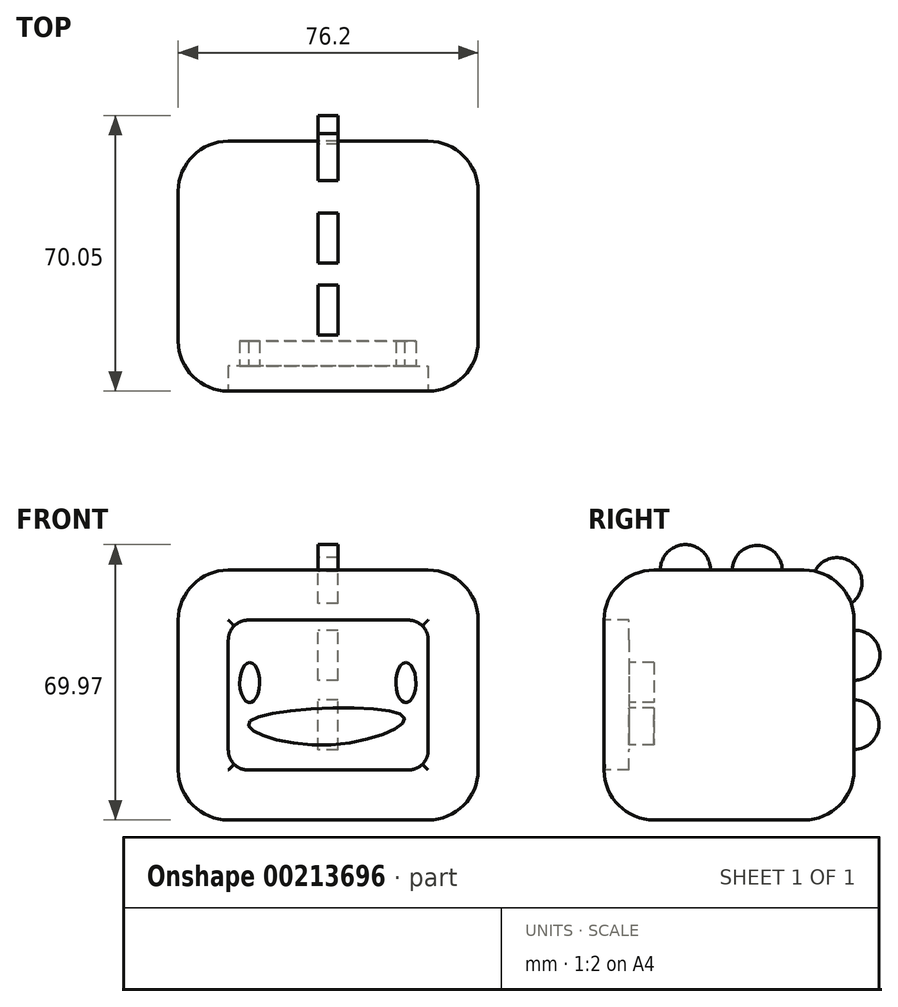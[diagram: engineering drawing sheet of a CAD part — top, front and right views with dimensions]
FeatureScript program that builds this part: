
annotation { "Feature Type Name" : "Feature", "Feature Type Description" : "" }
export const myFeature = defineFeature(function(context is Context, id is Id, definition is map)
    precondition{}
    {
        {
            var Q0;
            Q0=qCreatedBy(makeId("Top.planeOp"),FACE);
            var sketch = newSketch(context, id + "F0", { "sketchPlane" : qUnion([Q0])});
            skLineSegment(sketch, "E0.bottom", {"start": v(25.4, 31.75) * mm, "end": v(-25.4, 31.75) * mm});
            skLineSegment(sketch, "E0.top", {"start": v(25.4, -31.75) * mm, "end": v(-25.4, -31.75) * mm});
            skLineSegment(sketch, "E0.left", {"start": v(38.1, 19.05) * mm, "end": v(38.1, -19.05) * mm});
            skLineSegment(sketch, "E0.right", {"start": v(-38.1, 19.05) * mm, "end": v(-38.1, -19.05) * mm});
            skPoint(sketch, "E0.middle", {"position": v(0, 0) * mm});
            skPoint(sketch, "E1.visualSharp", {"position": v(38.1, -31.75) * mm});
            skArc(sketch, "E1.filletArc", {"start": v(25.4, -31.75) * mm, "mid": v(34.38, -28.03) * mm, "end": v(38.1, -19.05) * mm});
            skPoint(sketch, "E2.visualSharp", {"position": v(38.1, 31.75) * mm});
            skArc(sketch, "E2.filletArc", {"start": v(38.1, 19.05) * mm, "mid": v(34.38, 28.03) * mm, "end": v(25.4, 31.75) * mm});
            skPoint(sketch, "E3.visualSharp", {"position": v(-38.1, 31.75) * mm});
            skArc(sketch, "E3.filletArc", {"start": v(-25.4, 31.75) * mm, "mid": v(-34.38, 28.03) * mm, "end": v(-38.1, 19.05) * mm});
            skPoint(sketch, "E4.visualSharp", {"position": v(-38.1, -31.75) * mm});
            skArc(sketch, "E4.filletArc", {"start": v(-38.1, -19.05) * mm, "mid": v(-34.38, -28.03) * mm, "end": v(-25.4, -31.75) * mm});
            skSolve(sketch);
        }
        {
            var Q0;
            Q0=makeQuery(id+"F0.imprint","IMPRINT",FACE,{"disambiguationData":[TD([[makeQuery(id+"F0.imprint","IMPRINT",EDGE,{"derivedFrom":sQuery(id+"F0.wireOp",EDGE,"E0.bottom")}),1.0]])]});
            extrude(context, id + "F1", {"entities" : qUnion([Q0]), "depth" : 63.5 * mm});
        }
        {
            var Q0;
            Q0=makeQuery(id+"F1.opExtrude","CAP_FACE",FACE,{"disambiguationData":[OSD([sQuery(id+"F0.wireOp",EDGE,"E0.bottom"),sQuery(id+"F0.wireOp",EDGE,"E0.top"),sQuery(id+"F0.wireOp",EDGE,"E0.left"),sQuery(id+"F0.wireOp",EDGE,"E0.right"),sQuery(id+"F0.wireOp",EDGE,"E1.filletArc"),sQuery(id+"F0.wireOp",EDGE,"E2.filletArc"),sQuery(id+"F0.wireOp",EDGE,"E3.filletArc"),sQuery(id+"F0.wireOp",EDGE,"E4.filletArc")])],"isStart":false});
            var Q1;
            Q1=makeQuery(id+"F1.opExtrude","CAP_FACE",FACE,{"disambiguationData":[OSD([sQuery(id+"F0.wireOp",EDGE,"E0.bottom"),sQuery(id+"F0.wireOp",EDGE,"E0.top"),sQuery(id+"F0.wireOp",EDGE,"E0.left"),sQuery(id+"F0.wireOp",EDGE,"E0.right"),sQuery(id+"F0.wireOp",EDGE,"E1.filletArc"),sQuery(id+"F0.wireOp",EDGE,"E2.filletArc"),sQuery(id+"F0.wireOp",EDGE,"E3.filletArc"),sQuery(id+"F0.wireOp",EDGE,"E4.filletArc")])],"isStart":true});
            fillet(context, id + "F2", {"entities" : qUnion([Q0, Q1]), "radius" : 12.7 * mm, "tangentPropagation" : true, "allowEdgeOverflow" : false});
        }
        {
            var Q0;
            Q0=makeQuery(id+"F1.opExtrude","SWEPT_FACE",FACE,{"disambiguationData":[OSD([sQuery(id+"F0.wireOp",EDGE,"E0.top")])]});
            extrude(context, id + "F3", {"entities" : qUnion([Q0]), "operationType" : NewBodyOperationType.REMOVE, "oppositeDirection" : true, "depth" : 6.35 * mm});
        }
        {
            var Q0;
            {var subQ0=sQuery(id+"F0.wireOp",EDGE,"E4.filletArc");var subQ1=sQuery(id+"F0.wireOp",EDGE,"E0.top");Q0=makeQuery(id+"F3.boolean.opBoolean","COPY",EDGE,{"derivedFrom":makeQuery(id+"F3.opExtrude","SWEPT_EDGE",EDGE,{"disambiguationData":[OSD([subQ1,subQ0]),TDD([makeQuery(id+"F2.opFillet","BLEND_VERTEX",VERTEX,{"blendedFrom":[makeQuery(id+"F1.opExtrude","CAP_EDGE",EDGE,{"disambiguationData":[OSD([subQ1])],"isStart":false}),makeQuery(id+"F1.opExtrude","CAP_EDGE",EDGE,{"disambiguationData":[OSD([subQ0])],"isStart":false}),makeQuery(id+"F1.opExtrude","SWEPT_FACE",FACE,{"disambiguationData":[OSD([subQ1])]}),makeQuery(id+"F1.opExtrude","SWEPT_FACE",FACE,{"disambiguationData":[OSD([subQ0])]})],"blendedInto":[makeQuery(id+"F1.opExtrude","SWEPT_FACE",FACE,{"disambiguationData":[OSD([subQ1])]}),makeQuery(id+"F1.opExtrude","SWEPT_FACE",FACE,{"disambiguationData":[OSD([subQ0])]})]})])]})});}
            var Q1;
            {var subQ0=sQuery(id+"F0.wireOp",EDGE,"E4.filletArc");var subQ1=sQuery(id+"F0.wireOp",EDGE,"E0.top");Q1=makeQuery(id+"F3.boolean.opBoolean","COPY",EDGE,{"derivedFrom":makeQuery(id+"F3.opExtrude","SWEPT_EDGE",EDGE,{"disambiguationData":[OSD([subQ1,subQ0]),TDD([makeQuery(id+"F2.opFillet","BLEND_VERTEX",VERTEX,{"blendedFrom":[makeQuery(id+"F1.opExtrude","CAP_EDGE",EDGE,{"disambiguationData":[OSD([subQ1])],"isStart":true}),makeQuery(id+"F1.opExtrude","CAP_EDGE",EDGE,{"disambiguationData":[OSD([subQ0])],"isStart":true}),makeQuery(id+"F1.opExtrude","SWEPT_FACE",FACE,{"disambiguationData":[OSD([subQ1])]}),makeQuery(id+"F1.opExtrude","SWEPT_FACE",FACE,{"disambiguationData":[OSD([subQ0])]})],"blendedInto":[makeQuery(id+"F1.opExtrude","SWEPT_FACE",FACE,{"disambiguationData":[OSD([subQ1])]}),makeQuery(id+"F1.opExtrude","SWEPT_FACE",FACE,{"disambiguationData":[OSD([subQ0])]})]})])]})});}
            var Q2;
            {var subQ0=sQuery(id+"F0.wireOp",EDGE,"E1.filletArc");var subQ1=sQuery(id+"F0.wireOp",EDGE,"E0.top");Q2=makeQuery(id+"F3.boolean.opBoolean","COPY",EDGE,{"derivedFrom":makeQuery(id+"F3.opExtrude","SWEPT_EDGE",EDGE,{"disambiguationData":[OSD([subQ1,subQ0]),TDD([makeQuery(id+"F2.opFillet","BLEND_VERTEX",VERTEX,{"blendedFrom":[makeQuery(id+"F1.opExtrude","CAP_EDGE",EDGE,{"disambiguationData":[OSD([subQ1])],"isStart":false}),makeQuery(id+"F1.opExtrude","CAP_EDGE",EDGE,{"disambiguationData":[OSD([subQ0])],"isStart":false}),makeQuery(id+"F1.opExtrude","SWEPT_FACE",FACE,{"disambiguationData":[OSD([subQ1])]}),makeQuery(id+"F1.opExtrude","SWEPT_FACE",FACE,{"disambiguationData":[OSD([subQ0])]})],"blendedInto":[makeQuery(id+"F1.opExtrude","SWEPT_FACE",FACE,{"disambiguationData":[OSD([subQ1])]}),makeQuery(id+"F1.opExtrude","SWEPT_FACE",FACE,{"disambiguationData":[OSD([subQ0])]})]})])]})});}
            var Q3;
            {var subQ0=sQuery(id+"F0.wireOp",EDGE,"E1.filletArc");var subQ1=sQuery(id+"F0.wireOp",EDGE,"E0.top");Q3=makeQuery(id+"F3.boolean.opBoolean","COPY",EDGE,{"derivedFrom":makeQuery(id+"F3.opExtrude","SWEPT_EDGE",EDGE,{"disambiguationData":[OSD([subQ1,subQ0]),TDD([makeQuery(id+"F2.opFillet","BLEND_VERTEX",VERTEX,{"blendedFrom":[makeQuery(id+"F1.opExtrude","CAP_EDGE",EDGE,{"disambiguationData":[OSD([subQ1])],"isStart":true}),makeQuery(id+"F1.opExtrude","CAP_EDGE",EDGE,{"disambiguationData":[OSD([subQ0])],"isStart":true}),makeQuery(id+"F1.opExtrude","SWEPT_FACE",FACE,{"disambiguationData":[OSD([subQ1])]}),makeQuery(id+"F1.opExtrude","SWEPT_FACE",FACE,{"disambiguationData":[OSD([subQ0])]})],"blendedInto":[makeQuery(id+"F1.opExtrude","SWEPT_FACE",FACE,{"disambiguationData":[OSD([subQ1])]}),makeQuery(id+"F1.opExtrude","SWEPT_FACE",FACE,{"disambiguationData":[OSD([subQ0])]})]})])]})});}
            fillet(context, id + "F4", {"entities" : qUnion([Q0, Q1, Q2, Q3]), "radius" : 5.08 * mm, "tangentPropagation" : true, "allowEdgeOverflow" : false});
        }
        {
            var Q0;
            Q0=qCreatedBy(makeId("Front.planeOp"),FACE);
            cPlane(context, id + "F5", {"entities" : qUnion([Q0]), "cplaneType" : CPlaneType.OFFSET, "offset" : 25.4 * mm, "width" : 152.4 * mm, "height" : 152.4 * mm});
        }
        {
            var Q0;
            Q0=qCreatedBy(id+"F5.planeOp",FACE);
            var sketch = newSketch(context, id + "F6", { "sketchPlane" : qUnion([Q0])});
            skEllipse(sketch, "E5", {"center": v(-19.95, 34.96) * mm, "majorRadius": 5.08 * mm, "minorRadius": 2.54 * mm, "majorAxis": v(0, 1)});
            skEllipse(sketch, "E6", {"center": v(19.72, 34.9) * mm, "majorRadius": 5.08 * mm, "minorRadius": 2.54 * mm, "majorAxis": v(0, 1)});
            skSolve(sketch);
        }
        {
            var Q0;
            Q0=makeQuery(id+"F6.imprint","IMPRINT",FACE,{"disambiguationData":[TD([[makeQuery(id+"F6.imprint","IMPRINT",EDGE,{"derivedFrom":sQuery(id+"F6.wireOp",EDGE,"E5")}),1.0]])]});
            var Q1;
            Q1=makeQuery(id+"F6.imprint","IMPRINT",FACE,{"disambiguationData":[TD([[makeQuery(id+"F6.imprint","IMPRINT",EDGE,{"derivedFrom":sQuery(id+"F6.wireOp",EDGE,"E6")}),1.0]])]});
            extrude(context, id + "F7", {"entities" : qUnion([Q0, Q1]), "operationType" : NewBodyOperationType.REMOVE, "oppositeDirection" : true, "depth" : 6.35 * mm});
        }
        {
            var Q0;
            Q0=qCreatedBy(id+"F5.planeOp",FACE);
            var sketch = newSketch(context, id + "F8", { "sketchPlane" : qUnion([Q0])});
            skFitSpline(sketch, "E7", {"points": [v(-19.82, 25.16) * mm, v(0, 19.1) * mm, v(18.87, 26.57) * mm, v(-19.82, 25.16) * mm]});
            skSolve(sketch);
        }
        {
            var Q0;
            Q0 = qSketchRegion(id + "F8", true);
            extrude(context, id + "F9", {"entities" : qUnion([Q0]), "operationType" : NewBodyOperationType.REMOVE, "oppositeDirection" : true, "depth" : 6.35 * mm});
        }
        {
            var Q0;
            Q0=qCreatedBy(makeId("Right.planeOp"),FACE);
            var sketch = newSketch(context, id + "F10", { "sketchPlane" : qUnion([Q0])});
            skCircle(sketch, "E8", {"center": v(-11.1, 63.62) * mm, "radius": 6.35 * mm});
            skCircle(sketch, "E9", {"center": v(7.13, 63.44) * mm, "radius": 6.35 * mm});
            skCircle(sketch, "E10", {"center": v(27.4, 60.32) * mm, "radius": 6.35 * mm});
            skCircle(sketch, "E11", {"center": v(31.95, 41.87) * mm, "radius": 6.35 * mm});
            skCircle(sketch, "E12", {"center": v(31.68, 24.23) * mm, "radius": 6.35 * mm});
            skSolve(sketch);
        }
        {
            var Q0;
            Q0 = qSketchRegion(id + "F10", true);
            extrude(context, id + "F11", {"entities" : qUnion([Q0]), "operationType" : NewBodyOperationType.ADD, "depth" : 2.54 * mm, "hasSecondDirection" : true, "secondDirectionOppositeDirection" : true, "secondDirectionDepth" : 2.54 * mm});
        }
    });
